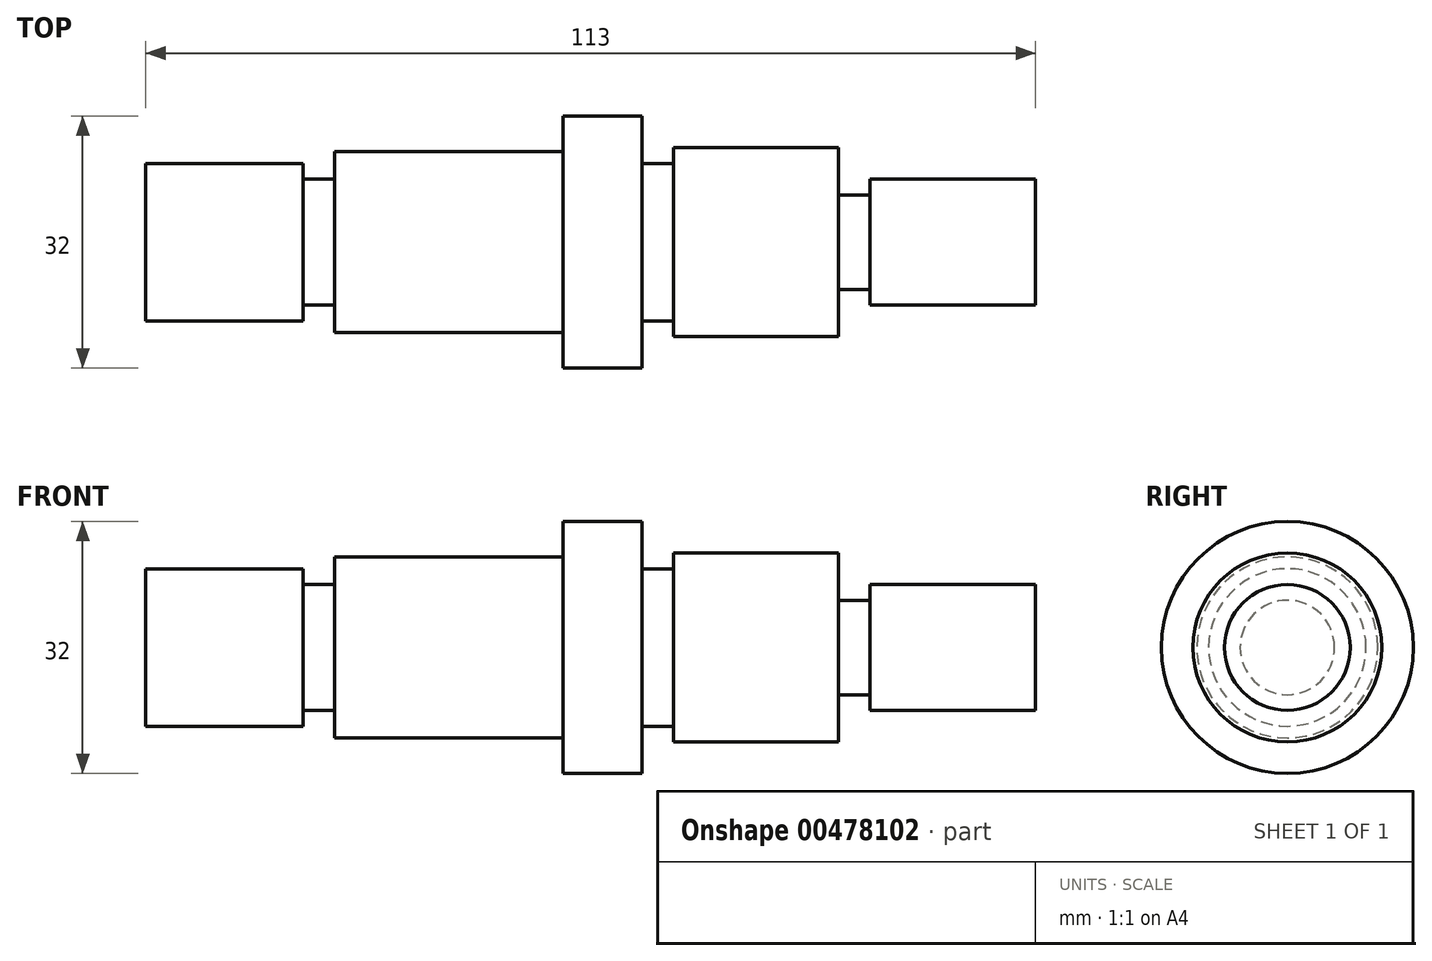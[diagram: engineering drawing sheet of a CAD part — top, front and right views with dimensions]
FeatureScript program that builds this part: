
annotation { "Feature Type Name" : "Feature", "Feature Type Description" : "" }
export const myFeature = defineFeature(function(context is Context, id is Id, definition is map)
    precondition{}
    {
        {
            var Q0;
            Q0=qCreatedBy(makeId("Front.planeOp"),FACE);
            var sketch = newSketch(context, id + "F0", { "sketchPlane" : qUnion([Q0])});
            skLineSegment(sketch, "E0.bottom", {"start": v(0, 0) * mm, "end": v(20, 0) * mm});
            skLineSegment(sketch, "E0.top", {"start": v(0, -10) * mm, "end": v(20, -10) * mm});
            skLineSegment(sketch, "E0.left", {"start": v(0, 0) * mm, "end": v(0, -10) * mm});
            skLineSegment(sketch, "E0.right", {"start": v(20, 0) * mm, "end": v(20, -10) * mm});
            skLineSegment(sketch, "E1.bottom", {"start": v(20, 0) * mm, "end": v(24, 0) * mm});
            skLineSegment(sketch, "E1.top", {"start": v(20, -8) * mm, "end": v(24, -8) * mm});
            skLineSegment(sketch, "E1.left", {"start": v(20, 0) * mm, "end": v(20, -8) * mm});
            skLineSegment(sketch, "E1.right", {"start": v(24, 0) * mm, "end": v(24, -8) * mm});
            skLineSegment(sketch, "E2.bottom", {"start": v(24, 0) * mm, "end": v(53, 0) * mm});
            skLineSegment(sketch, "E2.top", {"start": v(24, -11.5) * mm, "end": v(53, -11.5) * mm});
            skLineSegment(sketch, "E2.left", {"start": v(24, 0) * mm, "end": v(24, -11.5) * mm});
            skLineSegment(sketch, "E2.right", {"start": v(53, 0) * mm, "end": v(53, -11.5) * mm});
            skLineSegment(sketch, "E3.bottom", {"start": v(53, 0) * mm, "end": v(63, 0) * mm});
            skLineSegment(sketch, "E3.top", {"start": v(53, -16) * mm, "end": v(63, -16) * mm});
            skLineSegment(sketch, "E3.left", {"start": v(53, 0) * mm, "end": v(53, -16) * mm});
            skLineSegment(sketch, "E3.right", {"start": v(63, 0) * mm, "end": v(63, -16) * mm});
            skLineSegment(sketch, "E4.bottom", {"start": v(63, 0) * mm, "end": v(67, 0) * mm});
            skLineSegment(sketch, "E4.top", {"start": v(63, -10) * mm, "end": v(67, -10) * mm});
            skLineSegment(sketch, "E4.left", {"start": v(63, 0) * mm, "end": v(63, -10) * mm});
            skLineSegment(sketch, "E4.right", {"start": v(67, 0) * mm, "end": v(67, -10) * mm});
            skLineSegment(sketch, "E5.bottom", {"start": v(67, 0) * mm, "end": v(88, 0) * mm});
            skLineSegment(sketch, "E5.top", {"start": v(67, -12) * mm, "end": v(88, -12) * mm});
            skLineSegment(sketch, "E5.left", {"start": v(67, 0) * mm, "end": v(67, -12) * mm});
            skLineSegment(sketch, "E5.right", {"start": v(88, 0) * mm, "end": v(88, -12) * mm});
            skLineSegment(sketch, "E6.bottom", {"start": v(88, 0) * mm, "end": v(92, 0) * mm});
            skLineSegment(sketch, "E6.top", {"start": v(88, -6) * mm, "end": v(92, -6) * mm});
            skLineSegment(sketch, "E6.left", {"start": v(88, 0) * mm, "end": v(88, -6) * mm});
            skLineSegment(sketch, "E6.right", {"start": v(92, 0) * mm, "end": v(92, -6) * mm});
            skLineSegment(sketch, "E7.bottom", {"start": v(92, 0) * mm, "end": v(113, 0) * mm});
            skLineSegment(sketch, "E7.top", {"start": v(92, -8) * mm, "end": v(113, -8) * mm});
            skLineSegment(sketch, "E7.left", {"start": v(92, 0) * mm, "end": v(92, -8) * mm});
            skLineSegment(sketch, "E7.right", {"start": v(113, 0) * mm, "end": v(113, -8) * mm});
            skSolve(sketch);
        }
        {
            var Q0;
            Q0=makeQuery(id+"F0.imprint","IMPRINT",FACE,{"disambiguationData":[TD([[makeQuery(id+"F0.imprint","IMPRINT",EDGE,{"derivedFrom":sQuery(id+"F0.wireOp",EDGE,"E0.bottom")}),-1.0]])]});
            var Q1;
            {var subQ0=sQuery(id+"F0.wireOp",EDGE,"E1.bottom");Q1=makeQuery(id+"F0.imprint","IMPRINT",FACE,{"disambiguationData":[TD([[makeQuery(id+"F0.imprint","IMPRINT",EDGE,{"derivedFrom":subQ0}),-1.0]])]});}
            var Q2;
            {var subQ3=sQuery(id+"F0.wireOp",EDGE,"E2.bottom");Q2=makeQuery(id+"F0.imprint","IMPRINT",FACE,{"disambiguationData":[TD([[makeQuery(id+"F0.imprint","IMPRINT",EDGE,{"derivedFrom":subQ3}),-1.0]])]});}
            var Q3;
            {var subQ3=sQuery(id+"F0.wireOp",EDGE,"E3.bottom");Q3=makeQuery(id+"F0.imprint","IMPRINT",FACE,{"disambiguationData":[TD([[makeQuery(id+"F0.imprint","IMPRINT",EDGE,{"derivedFrom":subQ3}),-1.0]])]});}
            var Q4;
            {var subQ0=sQuery(id+"F0.wireOp",EDGE,"E4.bottom");Q4=makeQuery(id+"F0.imprint","IMPRINT",FACE,{"disambiguationData":[TD([[makeQuery(id+"F0.imprint","IMPRINT",EDGE,{"derivedFrom":subQ0}),-1.0]])]});}
            var Q5;
            {var subQ3=sQuery(id+"F0.wireOp",EDGE,"E5.bottom");Q5=makeQuery(id+"F0.imprint","IMPRINT",FACE,{"disambiguationData":[TD([[makeQuery(id+"F0.imprint","IMPRINT",EDGE,{"derivedFrom":subQ3}),-1.0]])]});}
            var Q6;
            {var subQ0=sQuery(id+"F0.wireOp",EDGE,"E6.bottom");Q6=makeQuery(id+"F0.imprint","IMPRINT",FACE,{"disambiguationData":[TD([[makeQuery(id+"F0.imprint","IMPRINT",EDGE,{"derivedFrom":subQ0}),-1.0]])]});}
            var Q7;
            {var subQ3=sQuery(id+"F0.wireOp",EDGE,"E7.bottom");Q7=makeQuery(id+"F0.imprint","IMPRINT",FACE,{"disambiguationData":[TD([[makeQuery(id+"F0.imprint","IMPRINT",EDGE,{"derivedFrom":subQ3}),-1.0]])]});}
            var Q8;
            Q8=sQuery(id+"F0.wireOp",EDGE,"E2.bottom");
            revolve(context, id + "F1", {"entities" : qUnion([Q0, Q1, Q2, Q3, Q4, Q5, Q6, Q7]), "axis" : qUnion([Q8]), "revolveType" : RevolveType.FULL});
        }
    });
